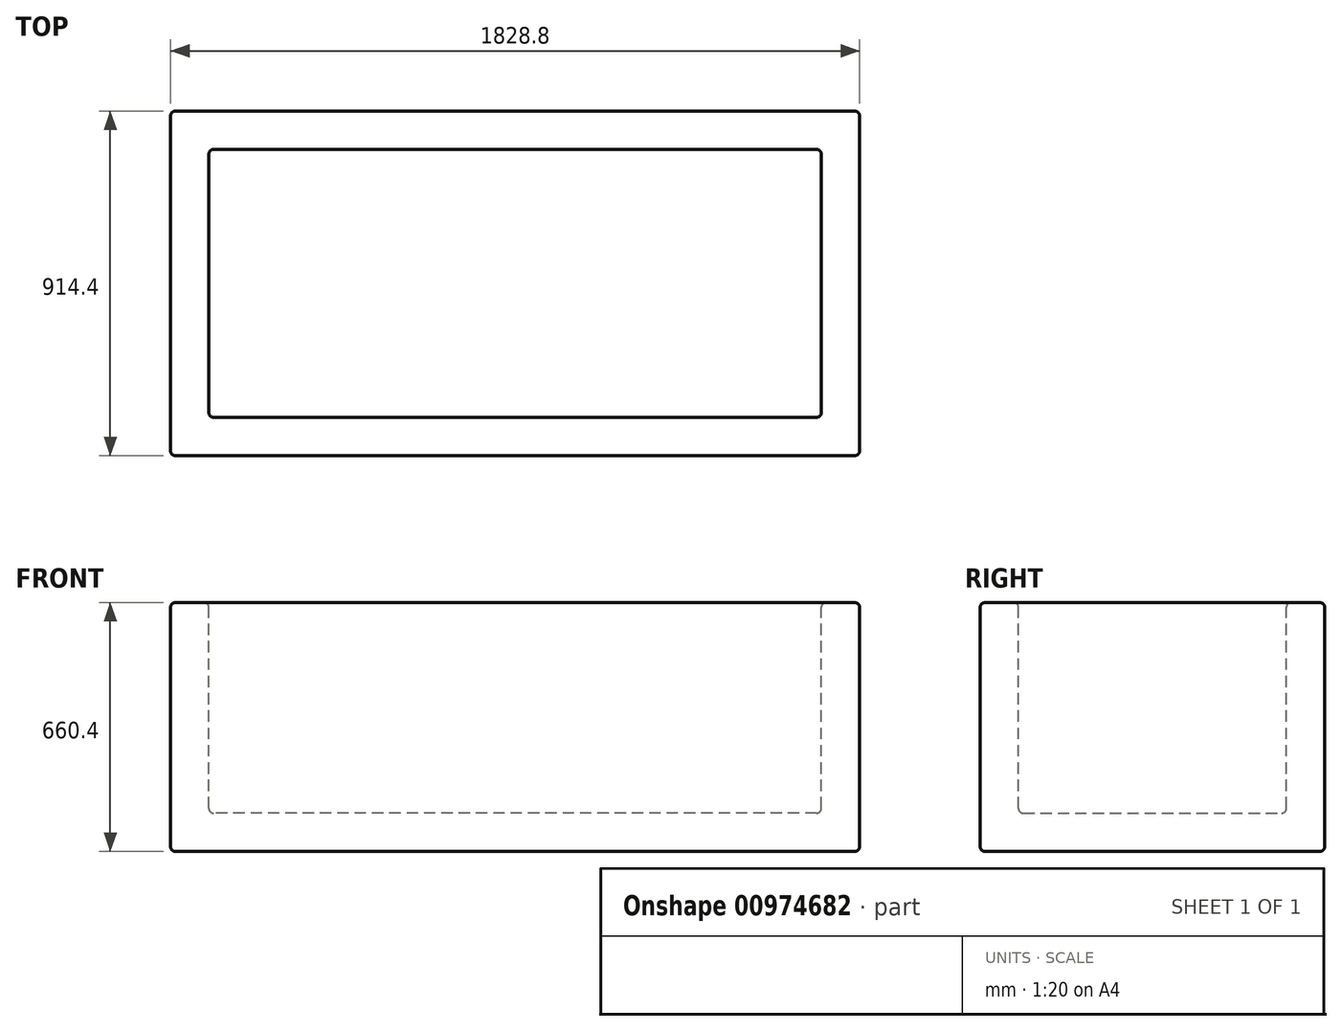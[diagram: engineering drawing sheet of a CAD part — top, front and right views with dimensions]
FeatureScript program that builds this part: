
annotation { "Feature Type Name" : "Feature", "Feature Type Description" : "" }
export const myFeature = defineFeature(function(context is Context, id is Id, definition is map)
    precondition{}
    {
        {
            var Q0;
            Q0=qCreatedBy(makeId("Top.planeOp"),FACE);
            var sketch = newSketch(context, id + "F0", { "sketchPlane" : qUnion([Q0])});
            skLineSegment(sketch, "E0.bottom", {"start": v(914.4, -457.2) * mm, "end": v(-914.4, -457.2) * mm});
            skLineSegment(sketch, "E0.top", {"start": v(914.4, 457.2) * mm, "end": v(-914.4, 457.2) * mm});
            skLineSegment(sketch, "E0.left", {"start": v(914.4, -457.2) * mm, "end": v(914.4, 457.2) * mm});
            skLineSegment(sketch, "E0.right", {"start": v(-914.4, -457.2) * mm, "end": v(-914.4, 457.2) * mm});
            skPoint(sketch, "E0.middle", {"position": v(0, 0) * mm});
            skSolve(sketch);
        }
        {
            var Q0;
            Q0=makeQuery(id+"F0.imprint","IMPRINT",FACE,{"disambiguationData":[TD([[makeQuery(id+"F0.imprint","IMPRINT",EDGE,{"derivedFrom":sQuery(id+"F0.wireOp",EDGE,"E0.bottom")}),-1.0]])]});
            extrude(context, id + "F1", {"entities" : qUnion([Q0]), "depth" : 660.4 * mm, "offsetDistance" : 25.4 * mm});
        }
        {
            var Q0;
            Q0=makeQuery(id+"F1.opExtrude","CAP_FACE",FACE,{"disambiguationData":[OSD([sQuery(id+"F0.wireOp",EDGE,"E0.bottom"),sQuery(id+"F0.wireOp",EDGE,"E0.top"),sQuery(id+"F0.wireOp",EDGE,"E0.left"),sQuery(id+"F0.wireOp",EDGE,"E0.right")])],"isStart":false});
            var sketch = newSketch(context, id + "F2", { "sketchPlane" : qUnion([Q0])});
            skLineSegment(sketch, "E1.bottom", {"start": v(812.8, -355.6) * mm, "end": v(-812.8, -355.6) * mm});
            skLineSegment(sketch, "E1.top", {"start": v(812.8, 355.6) * mm, "end": v(-812.8, 355.6) * mm});
            skLineSegment(sketch, "E1.left", {"start": v(812.8, -355.6) * mm, "end": v(812.8, 355.6) * mm});
            skLineSegment(sketch, "E1.right", {"start": v(-812.8, -355.6) * mm, "end": v(-812.8, 355.6) * mm});
            skPoint(sketch, "E1.middle", {"position": v(0, 0) * mm});
            skSolve(sketch);
        }
        {
            var Q0;
            Q0=makeQuery(id+"F2.imprint","IMPRINT",FACE,{"disambiguationData":[TD([[makeQuery(id+"F2.imprint","IMPRINT",EDGE,{"derivedFrom":sQuery(id+"F2.wireOp",EDGE,"E1.bottom")}),-1.0]])]});
            extrude(context, id + "F3", {"entities" : qUnion([Q0]), "operationType" : NewBodyOperationType.REMOVE, "oppositeDirection" : true, "depth" : 558.8 * mm, "offsetDistance" : 25.4 * mm});
        }
        {
            var Q0;
            Q0=makeQuery(id+"F3.boolean.opBoolean","COPY",FACE,{"derivedFrom":makeQuery(id+"F3.opExtrude","CAP_FACE",FACE,{"disambiguationData":[OSD([sQuery(id+"F2.wireOp",EDGE,"E1.bottom"),sQuery(id+"F2.wireOp",EDGE,"E1.top"),sQuery(id+"F2.wireOp",EDGE,"E1.left"),sQuery(id+"F2.wireOp",EDGE,"E1.right")])],"isStart":false})});
            var Q1;
            Q1=makeQuery(id+"F3.boolean.opBoolean","COPY",FACE,{"derivedFrom":makeQuery(id+"F3.opExtrude","SWEPT_FACE",FACE,{"disambiguationData":[OSD([sQuery(id+"F2.wireOp",EDGE,"E1.top")])]})});
            var Q2;
            Q2=makeQuery(id+"F3.boolean.opBoolean","COPY",FACE,{"derivedFrom":makeQuery(id+"F3.opExtrude","SWEPT_FACE",FACE,{"disambiguationData":[OSD([sQuery(id+"F2.wireOp",EDGE,"E1.right")])]})});
            var Q3;
            Q3=makeQuery(id+"F3.boolean.opBoolean","COPY",FACE,{"derivedFrom":makeQuery(id+"F3.opExtrude","SWEPT_FACE",FACE,{"disambiguationData":[OSD([sQuery(id+"F2.wireOp",EDGE,"E1.left")])]})});
            var Q4;
            Q4=makeQuery(id+"F3.boolean.opBoolean","COPY",FACE,{"derivedFrom":makeQuery(id+"F3.opExtrude","SWEPT_FACE",FACE,{"disambiguationData":[OSD([sQuery(id+"F2.wireOp",EDGE,"E1.bottom")])]})});
            var Q5;
            Q5=makeQuery(id+"F3.boolean.opBoolean","COPY",EDGE,{"derivedFrom":makeQuery(id+"F3.opExtrude","CAP_EDGE",EDGE,{"disambiguationData":[OSD([sQuery(id+"F2.wireOp",EDGE,"E1.top")])],"isStart":true})});
            var Q6;
            Q6=makeQuery(id+"F3.boolean.opBoolean","COPY",EDGE,{"derivedFrom":makeQuery(id+"F3.opExtrude","CAP_EDGE",EDGE,{"disambiguationData":[OSD([sQuery(id+"F2.wireOp",EDGE,"E1.left")])],"isStart":true})});
            var Q7;
            Q7=makeQuery(id+"F1.opExtrude","SWEPT_FACE",FACE,{"disambiguationData":[OSD([sQuery(id+"F0.wireOp",EDGE,"E0.bottom")])]});
            var Q8;
            Q8=makeQuery(id+"F1.opExtrude","SWEPT_FACE",FACE,{"disambiguationData":[OSD([sQuery(id+"F0.wireOp",EDGE,"E0.left")])]});
            var Q9;
            Q9=makeQuery(id+"F1.opExtrude","SWEPT_FACE",FACE,{"disambiguationData":[OSD([sQuery(id+"F0.wireOp",EDGE,"E0.top")])]});
            var Q10;
            Q10=makeQuery(id+"F1.opExtrude","SWEPT_FACE",FACE,{"disambiguationData":[OSD([sQuery(id+"F0.wireOp",EDGE,"E0.right")])]});
            fillet(context, id + "F4", {"entities" : qUnion([Q0, Q1, Q2, Q3, Q4, Q5, Q6, Q7, Q8, Q9, Q10]), "radius" : 12.7 * mm, "tangentPropagation" : true, "allowEdgeOverflow" : false});
        }
    });
